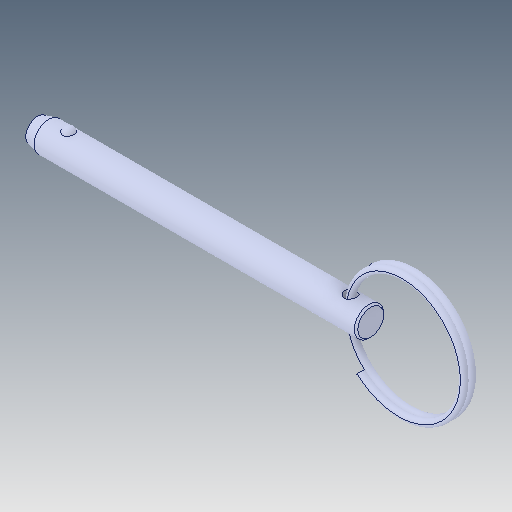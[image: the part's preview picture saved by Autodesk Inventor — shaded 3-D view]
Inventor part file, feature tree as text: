
AUTODESK INVENTOR PART (.ipt)
format: ipt  version: 2023.5 (Build 275446000, 446)  size: 216,064 bytes
history: native  units: in
note: dims shown in document units (in); Inventor stores cm internally (conversion verified against a paired STEP export)
features: revolve x1, other x1, sweep x1
ambient origin geometry x8: Origin, YZ Plane, XZ Plane, XY Plane, X Axis, Y Axis, Z Axis, Center Point
bodies: Solid1 (feature_tree), Solid2 (feature_tree), Solid3 (feature_tree)
feature tree (3):
  revolve  "Revolve2"  [1 undecoded]
  other  "Cut-Revolve2"
  sweep  "Sweep2"
note: 1 required parameter value undecoded (feature->parameter linkage not recoverable at this tier; creation-order binding heuristic only, values carry confidence <= 0.55)
